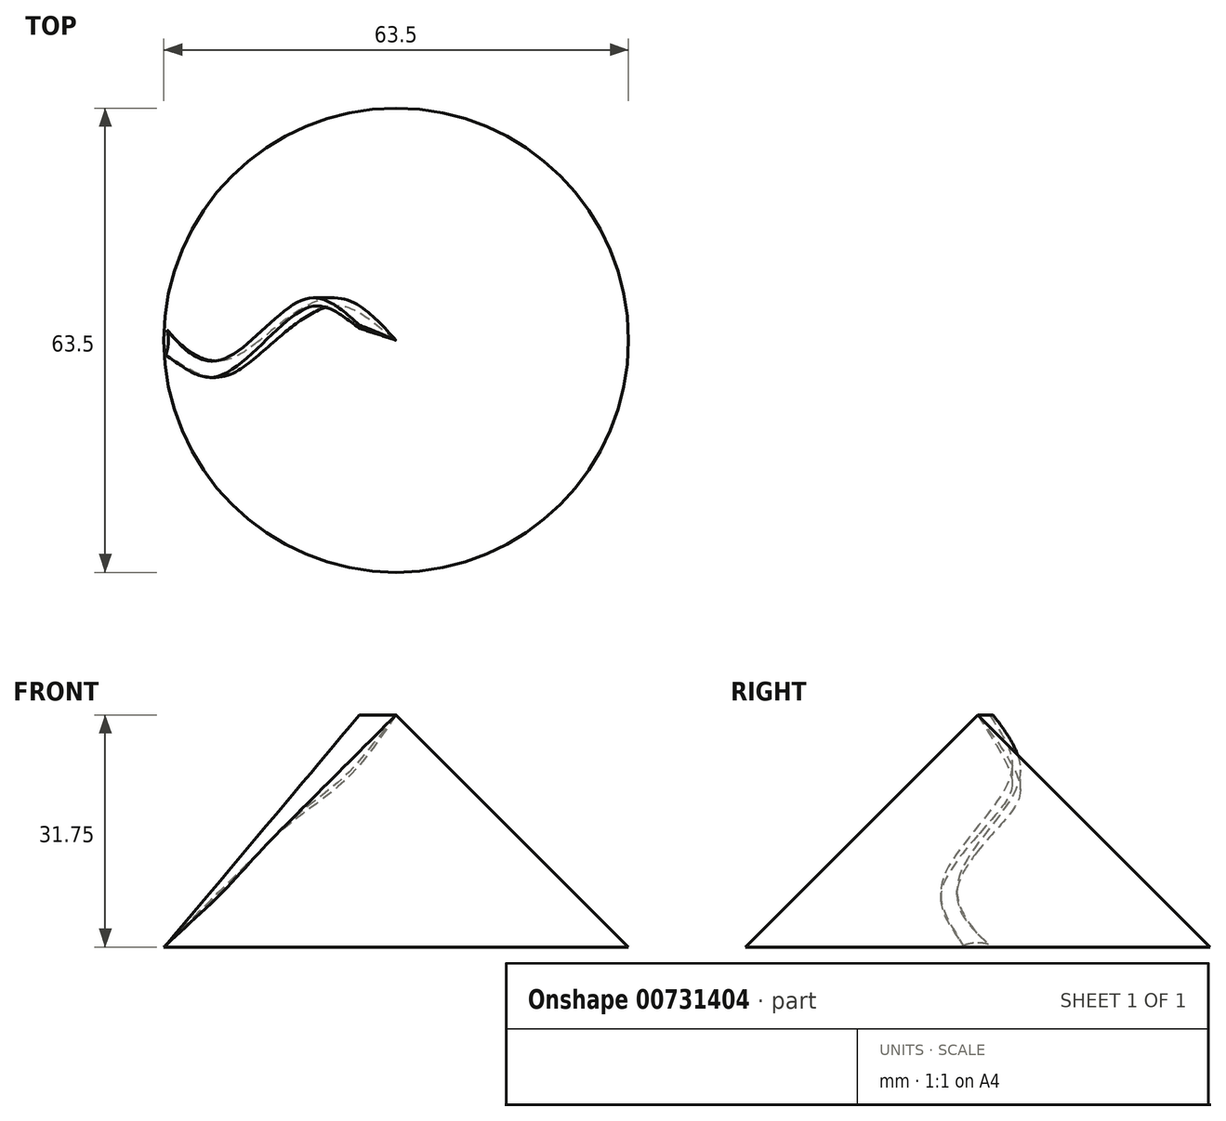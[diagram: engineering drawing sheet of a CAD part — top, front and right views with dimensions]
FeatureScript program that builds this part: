
annotation { "Feature Type Name" : "Feature", "Feature Type Description" : "" }
export const myFeature = defineFeature(function(context is Context, id is Id, definition is map)
    precondition{}
    {
        {
            var Q0;
            Q0=qCreatedBy(makeId("Front.planeOp"),FACE);
            var sketch = newSketch(context, id + "F0", { "sketchPlane" : qUnion([Q0])});
            skLineSegment(sketch, "E0", {"start": v(31.75, 0) * mm, "end": v(0, 0) * mm});
            skLineSegment(sketch, "E1", {"start": v(0, 0) * mm, "end": v(0, 31.75) * mm});
            skLineSegment(sketch, "E2", {"start": v(0, 31.75) * mm, "end": v(31.75, 0) * mm});
            skSolve(sketch);
        }
        {
            var Q0;
            Q0 = qSketchRegion(id + "F0", true);
            var Q1;
            Q1=sQuery(id+"F0.wireOp",EDGE,"E1");
            revolve(context, id + "F1", {"surfaceOperationType" : NewSurfaceOperationType.NEW, "entities" : qUnion([Q0]), "axis" : qUnion([Q1]), "revolveType" : RevolveType.FULL});
        }
        {
            var Q0;
            Q0=qCreatedBy(makeId("Top.planeOp"),FACE);
            var sketch = newSketch(context, id + "F2", { "sketchPlane" : qUnion([Q0])});
            skFitSpline(sketch, "E3", {"points": [v(13.16, 0) * mm, v(-2.9, 5.37) * mm, v(-19.38, -2.63) * mm, v(-31.65, 1.9) * mm], "startDerivative": vector(-63.87, 39.95) * mm, "endDerivative": vector(-38.3, 33.4) * mm});
            skFitSpline(sketch, "E4", {"points": [v(13.16, 0) * mm, v(-1.7, 4.31) * mm, v(-19.7, -4.8) * mm, v(-31.65, -1.9) * mm], "startDerivative": vector(-63.63, 29.6) * mm, "endDerivative": vector(-44.16, 19.2) * mm});
            skLineSegment(sketch, "E5", {"start": v(-31.65, -1.9) * mm, "end": v(-31.65, 1.9) * mm});
            skSolve(sketch);
        }
        {
            var Q0;
            Q0 = qSketchRegion(id + "F2", true);
            var Q1;
            Q1=sQuery(id+"F2.wireOp",EDGE,"E5");
            revolve(context, id + "F3", {"operationType" : NewBodyOperationType.ADD, "surfaceOperationType" : NewSurfaceOperationType.NEW, "entities" : qUnion([Q0]), "axis" : qUnion([Q1]), "revolveType" : RevolveType.ONE_DIRECTION, "oppositeDirection" : true, "angle" : 50 * degree});
        }
        {
            var Q0;
            Q0=makeQuery(id+"F1.opRevolve","SWEPT_FACE",FACE,{"disambiguationData":[OSD([sQuery(id+"F0.wireOp",EDGE,"E0")])]});
            var sketch = newSketch(context, id + "F4", { "sketchPlane" : qUnion([Q0])});
            skCircle(sketch, "E6", {"center": v(0, 0) * mm, "radius": 14.14 * mm});
            skSolve(sketch);
        }
        {
            var Q0;
            Q0 = qSketchRegion(id + "F4", true);
            extrude(context, id + "F5", {"entities" : qUnion([Q0]), "operationType" : NewBodyOperationType.REMOVE, "oppositeDirection" : true, "depth" : 38.1 * mm, "offsetDistance" : 25.4 * mm, "hasSecondDirection" : true, "secondDirectionOppositeDirection" : true, "secondDirectionDepth" : 31.75 * mm});
        }
    });
